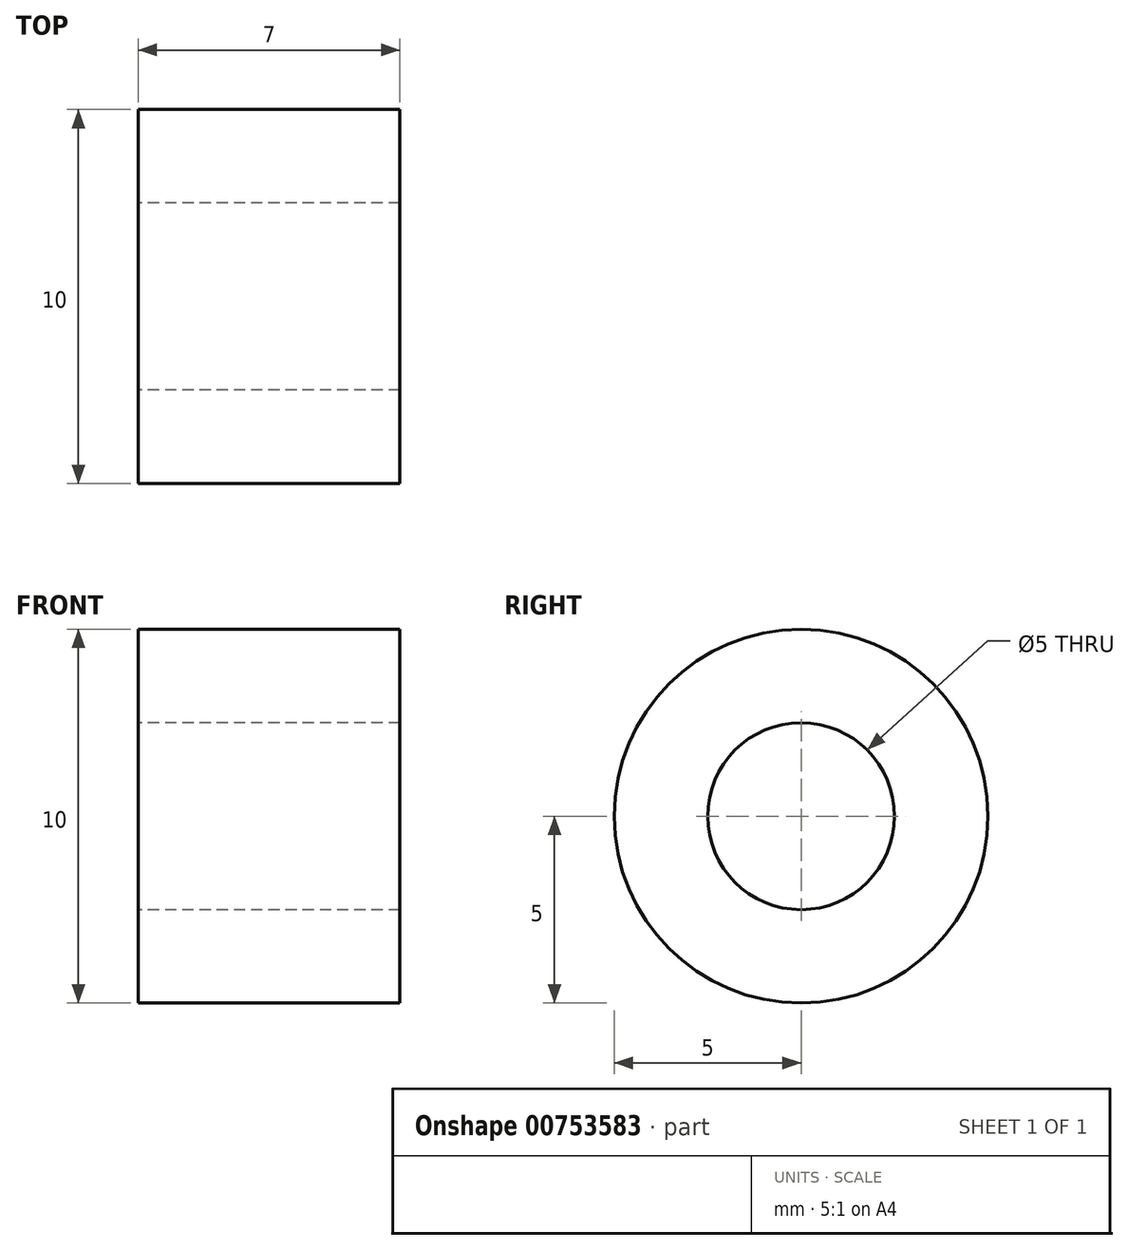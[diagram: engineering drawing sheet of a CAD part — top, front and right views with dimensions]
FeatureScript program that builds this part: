
annotation { "Feature Type Name" : "Feature", "Feature Type Description" : "" }
export const myFeature = defineFeature(function(context is Context, id is Id, definition is map)
    precondition{}
    {
        {
            var Q0;
            Q0=qCreatedBy(makeId("Right.planeOp"),FACE);
            var sketch = newSketch(context, id + "F0", { "sketchPlane" : qUnion([Q0])});
            skCircle(sketch, "E0", {"center": v(0, 0) * mm, "radius": 5 * mm});
            skCircle(sketch, "E1", {"center": v(0, 0) * mm, "radius": 2.5 * mm});
            skSolve(sketch);
        }
        {
            var Q0;
            Q0=makeQuery(id+"F0.imprint","IMPRINT",FACE,{"disambiguationData":[TD([[makeQuery(id+"F0.imprint","IMPRINT",EDGE,{"derivedFrom":sQuery(id+"F0.wireOp",EDGE,"E0")}),1.0]])]});
            extrude(context, id + "F1", {"entities" : qUnion([Q0]), "depth" : 7 * mm, "offsetDistance" : 25.4 * mm});
        }
    });
